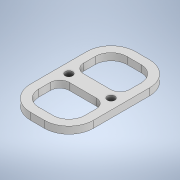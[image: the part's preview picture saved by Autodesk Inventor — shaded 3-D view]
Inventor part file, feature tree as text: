
AUTODESK INVENTOR PART (.ipt)
format: ipt  version: 2021 (Build 250183000, 183)  size: 162,304 bytes
history: native  units: mm
features: extrude x1, sketch x1
ambient origin geometry x8: Origin, YZ Plane, XZ Plane, XY Plane, X Axis, Y Axis, Z Axis, Center Point
bodies: Solid1 (feature_tree)
feature tree (2):
  extrude  "Extrusion1"  Depth=1.5mm
  sketch  "Sketch2"  dims[d8=1.0mm d9=1.0mm d10=2.6mm d11=23.2mm d12=14.2mm d13=8.0mm d15=23.2mm d16=0.4mm d17=0.4mm d18=2.0mm d19=2.0mm d20=1.6mm d21=1.6mm d22=2.2mm d23=2.2mm d24=1.5mm d25=0.0mm]
